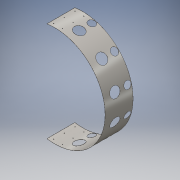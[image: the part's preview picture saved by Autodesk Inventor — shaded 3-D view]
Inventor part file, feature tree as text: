
AUTODESK INVENTOR PART (.ipt)
format: ipt  version: 2016 (Build 200138000, 138)  size: 724,480 bytes
history: native  units: mm
features: other x10, plane x10, sketch x9
ambient origin geometry x8: Origin, YZ Plane, XZ Plane, XY Plane, X Axis, Y Axis, Z Axis, Center Point
bodies: Body1 (feature_tree)
feature tree (29):
  other  "Contour Roll1"
  plane  "Work Plane32"
  plane  "Work Plane33"
  plane  "Work Plane34"
  plane  "Work Plane35"
  plane  "Work Plane36"
  plane  "Work Plane37"
  plane  "Work Plane38"
  plane  "Work Plane39"
  plane  "Work Plane40"
  plane  "Work Plane41"
  sketch  "Sketch4"  dims[d4=254.0mm]
  sketch  "Sketch30"  dims[d5=457.2mm]
  sketch  "Sketch31"  dims[d11=1.0mm]
  sketch  "Sketch32"  dims[d12=34.557519mm]
  sketch  "Sketch33"  dims[d13=1581.696917mm d14=457.699787mm]
  sketch  "Sketch34"  dims[d158=105.0deg]
  sketch  "Sketch35"  dims[d159=135.0deg]
  sketch  "Sketch36"  dims[d160=165.0deg]
  sketch  "Sketch37"  dims[d161=165.0deg d162=135.0deg d163=105.0deg d164=64.0mm d165=91.0mm d166=35.5mm d167=150.0mm d168=1.0mm d169=0.0mm d170=91.0mm d171=64.0mm d172=35.5mm d173=150.0mm d174=1.0mm d175=0.0mm d176=91.0mm d177=64.0mm d178=35.5mm d179=150.0mm d180=1.0mm d181=0.0mm d182=91.0mm d183=64.0mm d184=35.5mm d185=150.0mm d186=1.0mm d187=0.0mm d188=91.0mm d189=64.0mm d190=35.5mm d191=150.0mm d192=1.0mm d193=0.0mm d194=91.0mm d195=64.0mm d197=35.5mm d198=150.0mm d199=1.0mm d200=0.0mm d202=16.580628mm d203=14.835299mm d204=16.580628mm d205=14.835299mm d206=5.0mm d207=5.0mm d208=5.0mm d209=30.0mm d210=30.0mm d211=97.0mm d212=1.0mm d213=0.0mm d214=5.0mm d215=5.0mm d216=5.0mm d217=1.0mm d218=0.0mm d219=30.0mm d220=97.0mm d221=30.0mm]
  other  "Cut18"
  other  "Cut19"
  other  "Cut20"
  other  "Cut21"
  other  "Cut22"
  other  "Cut23"
  other  "Cut24"
  other  "Cut25"
  other  "Definition1"
